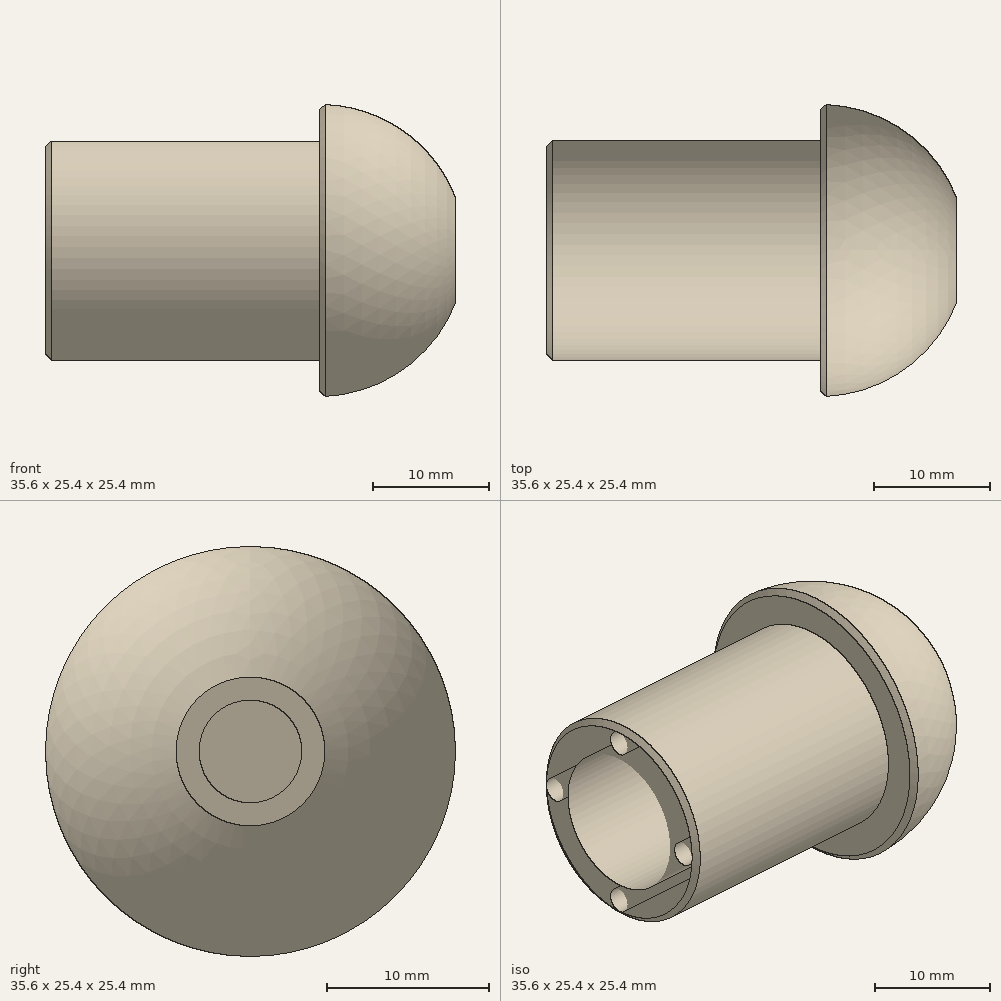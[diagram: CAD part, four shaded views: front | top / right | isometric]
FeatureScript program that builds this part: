
annotation { "Feature Type Name" : "Feature", "Feature Type Description" : "" }
export const myFeature = defineFeature(function(context is Context, id is Id, definition is map)
    precondition{}
    {
        {
            var Q0;
            Q0=qCreatedBy(makeId("Front.planeOp"),FACE);
            var sketch = newSketch(context, id + "F0", { "sketchPlane" : qUnion([Q0])});
            skLineSegment(sketch, "E0", {"start": v(-18.87, 0) * mm, "end": v(-6.1, 0) * mm});
            skLineSegment(sketch, "E1", {"start": v(0, 0) * mm, "end": v(0, 9.53) * mm});
            skLineSegment(sketch, "E2", {"start": v(0, 9.53) * mm, "end": v(23.81, 9.53) * mm});
            skLineSegment(sketch, "E3", {"start": v(23.81, 9.53) * mm, "end": v(23.81, 12.7) * mm});
            skPoint(sketch, "E4.centerSnap0", {"position": v(23.81, 11.11) * mm});
            skPoint(sketch, "E5.middle", {"position": v(39.41, 0) * mm});
            skLineSegment(sketch, "E6", {"start": v(36.28, 2.4) * mm, "end": v(36.28, 0) * mm});
            skLineSegment(sketch, "E7", {"start": v(36.28, 0) * mm, "end": v(0, 0) * mm});
            skArc(sketch, "E8", {"start": v(23.81, 12.7) * mm, "mid": v(31.9, 9.8) * mm, "end": v(36.28, 2.4) * mm});
            skSolve(sketch);
        }
        {
            var Q0;
            Q0=makeQuery(id+"F0.imprint","IMPRINT",FACE,{"disambiguationData":[TD([[makeQuery(id+"F0.imprint","IMPRINT",EDGE,{"derivedFrom":sQuery(id+"F0.wireOp",EDGE,"E1")}),-1.0]])]});
            var Q1;
            Q1=sQuery(id+"F0.wireOp",EDGE,"E7");
            revolve(context, id + "F1", {"entities" : qUnion([Q0]), "axis" : qUnion([Q1]), "revolveType" : RevolveType.FULL});
        }
        {
            var Q0;
            Q0=makeQuery(id+"F1.opRevolve","SWEPT_FACE",FACE,{"disambiguationData":[OSD([sQuery(id+"F0.wireOp",EDGE,"E6")])]});
            var sketch = newSketch(context, id + "F2", { "sketchPlane" : qUnion([Q0])});
            skCircle(sketch, "E9", {"center": v(0, 0) * mm, "radius": 3.18 * mm});
            skSolve(sketch);
        }
        {
            var Q0;
            Q0 = qSketchRegion(id + "F2", true);
            extrude(context, id + "F3", {"entities" : qUnion([Q0]), "operationType" : NewBodyOperationType.REMOVE, "oppositeDirection" : true, "depth" : 15.24 * mm});
        }
        {
            var Q0;
            Q0=makeQuery(id+"F3.boolean.opBoolean","COPY",FACE,{"derivedFrom":makeQuery(id+"F3.opExtrude","CAP_FACE",FACE,{"disambiguationData":[OSD([sQuery(id+"F2.wireOp",EDGE,"E9")])],"isStart":false})});
            cPlane(context, id + "F4", {"entities" : qUnion([Q0]), "cplaneType" : CPlaneType.OFFSET, "offset" : 15.24 * mm, "width" : 152.4 * mm, "height" : 152.4 * mm});
        }
        {
            var Q0;
            Q0=qCreatedBy(id+"F4.planeOp",FACE);
            var sketch = newSketch(context, id + "F5", { "sketchPlane" : qUnion([Q0])});
            skCircle(sketch, "E10", {"center": v(0, 0) * mm, "radius": 4.76 * mm});
            skSolve(sketch);
        }
        {
            var Q0;
            Q0 = qSketchRegion(id + "F5", true);
            extrude(context, id + "F6", {"entities" : qUnion([Q0]), "operationType" : NewBodyOperationType.REMOVE, "oppositeDirection" : true, "depth" : 0.64 * mm});
        }
        {
            var Q0;
            Q0=makeQuery(id+"F1.opRevolve","SWEPT_FACE",FACE,{"disambiguationData":[OSD([sQuery(id+"F0.wireOp",EDGE,"E1")])]});
            var sketch = newSketch(context, id + "F7", { "sketchPlane" : qUnion([Q0])});
            skCircle(sketch, "E11", {"center": v(0, 0) * mm, "radius": 6.35 * mm});
            skSolve(sketch);
        }
        {
            var Q0;
            Q0 = qSketchRegion(id + "F7", true);
            extrude(context, id + "F8", {"entities" : qUnion([Q0]), "operationType" : NewBodyOperationType.REMOVE, "oppositeDirection" : true, "depth" : 19.05 * mm});
        }
        {
            var Q0;
            Q0=makeQuery(id+"F1.opRevolve","SWEPT_EDGE",EDGE,{"disambiguationData":[OSD([sQuery(id+"F0.wireOp",EDGE,"E3"),sQuery(id+"F0.wireOp",EDGE,"E8")])]});
            var Q1;
            Q1=makeQuery(id+"F1.opRevolve","SWEPT_EDGE",EDGE,{"disambiguationData":[OSD([sQuery(id+"F0.wireOp",EDGE,"E1"),sQuery(id+"F0.wireOp",EDGE,"E2")])]});
            chamfer(context, id + "F9", {"entities" : qUnion([Q0, Q1]), "width" : 0.5 * mm, "tangentPropagation" : true});
        }
        {
            var Q0;
            Q0=makeQuery(id+"F1.opRevolve","SWEPT_FACE",FACE,{"disambiguationData":[OSD([sQuery(id+"F0.wireOp",EDGE,"E1")])]});
            var sketch = newSketch(context, id + "F10", { "sketchPlane" : qUnion([Q0])});
            skCircle(sketch, "E12", {"center": v(0, 7.94) * mm, "radius": 1.08 * mm});
            skCircle(sketch, "E13", {"center": v(0, -7.94) * mm, "radius": 1.08 * mm});
            skCircle(sketch, "E14", {"center": v(7.94, 0) * mm, "radius": 1.08 * mm});
            skCircle(sketch, "E15", {"center": v(-7.94, 0) * mm, "radius": 1.08 * mm});
            skSolve(sketch);
        }
        {
            var Q0;
            Q0 = qSketchRegion(id + "F10", true);
            extrude(context, id + "F11", {"entities" : qUnion([Q0]), "operationType" : NewBodyOperationType.REMOVE, "oppositeDirection" : true, "depth" : 9.52 * mm});
        }
    });
